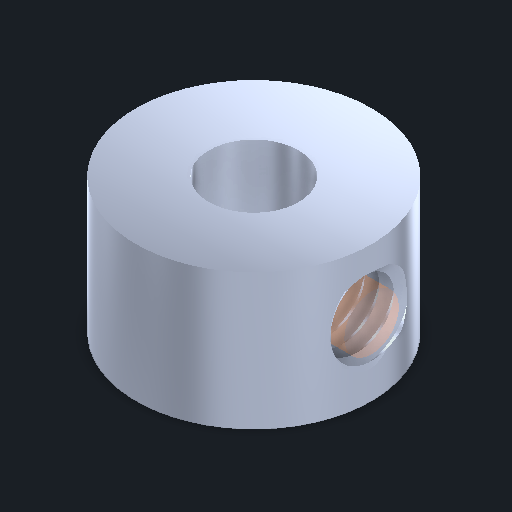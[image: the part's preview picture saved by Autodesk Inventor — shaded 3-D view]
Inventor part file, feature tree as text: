
AUTODESK INVENTOR PART (.ipt)
format: ipt  version: 2024 (Build 280153000, 153)  size: 613,888 bytes
history: native  units: in
note: dims shown in document units (in); Inventor stores cm internally (conversion verified against a paired STEP export)
features: extrude x3, other x2, sketch x2, imported_body x1, plane x1
ambient origin geometry x8: Origin, YZ Plane, XZ Plane, XY Plane, X Axis, Y Axis, Z Axis, Center Point
bodies: Body1 (feature_tree), Body2 (feature_tree)
feature tree (9):
  parser-record x1  (decoder bookkeeping rows leaked as tree rows — omitted from the tree; the rows remain in map.json)
  imported_body  "Base1"
  extrude  "Extrusion1"  Depth=0.005in TaperAngle=0.0deg
  extrude  "Extrusion2"  Depth=1.0in TaperAngle=0.0deg
  plane  "Work Plane1"
  sketch  "Sketch1"  dims[d3=0.005in d4=0.0in d5=0.005in d6=0.0in]
  sketch  "Sketch2"  dims[d7=0.1in d8=1.0in d9=0.0in]
  other  "Srf1"
  extrude  "ExtrusionSrf1"  [1 undecoded]
note: 1 required parameter value undecoded (feature->parameter linkage not recoverable at this tier; creation-order binding heuristic only, values carry confidence <= 0.55)
